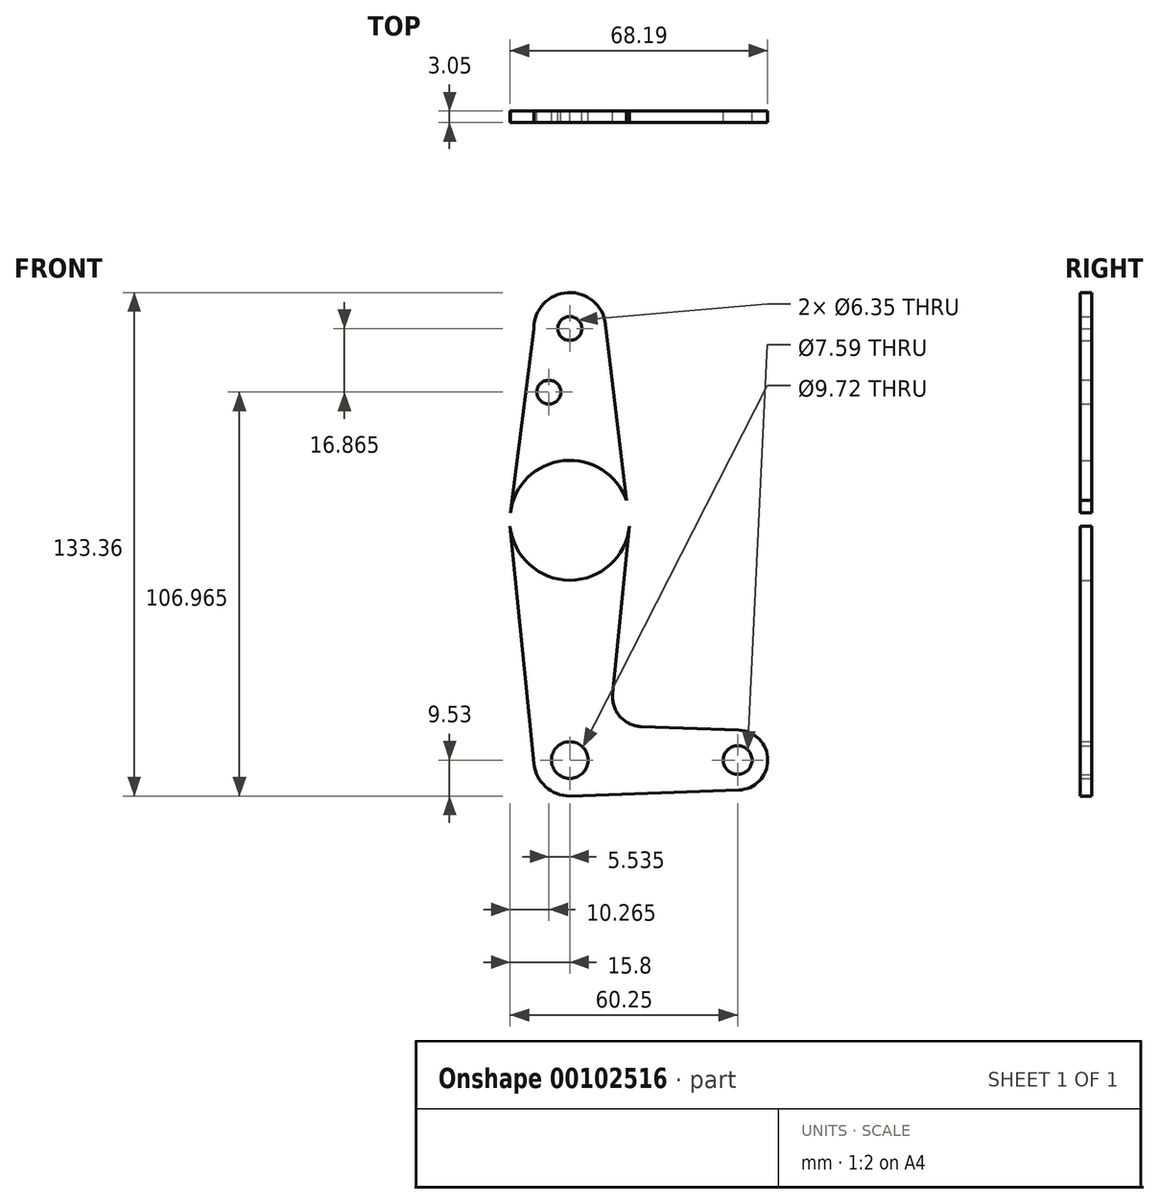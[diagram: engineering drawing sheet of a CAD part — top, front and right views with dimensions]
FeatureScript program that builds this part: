
annotation { "Feature Type Name" : "Feature", "Feature Type Description" : "" }
export const myFeature = defineFeature(function(context is Context, id is Id, definition is map)
    precondition{}
    {
        {
            var Q0;
            Q0=qCreatedBy(makeId("Front.planeOp"),FACE);
            var sketch = newSketch(context, id + "F0", { "sketchPlane" : qUnion([Q0])});
            skLineSegment(sketch, "E0", {"start": v(0, 114.3) * mm, "end": v(0, 0) * mm});
            skLineSegment(sketch, "E1", {"start": v(0, 0) * mm, "end": v(83.2, 0) * mm});
            skCircle(sketch, "E2", {"center": v(0, 114.3) * mm, "radius": 9.53 * mm});
            skCircle(sketch, "E3", {"center": v(0, 63.5) * mm, "radius": 15.88 * mm});
            skCircle(sketch, "E4", {"center": v(44.45, 0) * mm, "radius": 7.94 * mm});
            skCircle(sketch, "E5", {"center": v(0, 0) * mm, "radius": 9.53 * mm});
            skLineSegment(sketch, "E6", {"start": v(15.8, 61.91) * mm, "end": v(11.34, 17.59) * mm});
            skLineSegment(sketch, "E7", {"start": v(15.8, 61.91) * mm, "end": v(9.46, 115.42) * mm});
            skLineSegment(sketch, "E8", {"start": v(-9.53, 114.3) * mm, "end": v(-15.75, 65.5) * mm});
            skLineSegment(sketch, "E9", {"start": v(-15.8, 61.91) * mm, "end": v(-9.48, -0.95) * mm});
            skLineSegment(sketch, "E10", {"start": v(18.97, 8.85) * mm, "end": v(44.73, 7.93) * mm});
            skLineSegment(sketch, "E11", {"start": v(0, -9.53) * mm, "end": v(44.73, -7.93) * mm});
            skCircle(sketch, "E12", {"center": v(-5.53, 97.43) * mm, "radius": 3.18 * mm});
            skCircle(sketch, "E13", {"center": v(0, 114.3) * mm, "radius": 3.18 * mm});
            skCircle(sketch, "E14", {"center": v(0, 63.5) * mm, "radius": 1.59 * mm});
            skCircle(sketch, "E15", {"center": v(0, 0) * mm, "radius": 4.86 * mm});
            skCircle(sketch, "E16", {"center": v(44.45, 0) * mm, "radius": 3.8 * mm});
            skArc(sketch, "E17.filletArc", {"start": v(11.34, 17.59) * mm, "mid": v(13.26, 11.57) * mm, "end": v(18.97, 8.85) * mm});
            skSolve(sketch);
        }
        {
            var Q0;
            {var subQ0=sQuery(id+"F0.wireOp",EDGE,"E2");var subQ1=sQuery(id+"F0.wireOp",EDGE,"E0");var subQ2=makeQuery(id+"F0.imprint","INTERSECT",VERTEX,{"derivedFrom":[subQ1,subQ0]});Q0=makeQuery(id+"F0.imprint","IMPRINT",FACE,{"disambiguationData":[TD([[makeQuery(id+"F0.imprint","IMPRINT",EDGE,{"disambiguationData":[TD([[subQ2,-1.0]])],"derivedFrom":subQ1}),1.0]])]});}
            var Q1;
            Q1=makeQuery(id+"F0.imprint","IMPRINT",FACE,{"disambiguationData":[TD([[makeQuery(id+"F0.imprint","IMPRINT",EDGE,{"derivedFrom":sQuery(id+"F0.wireOp",EDGE,"E13")}),-1.0]])]});
            var Q2;
            {var subQ1=sQuery(id+"F0.wireOp",EDGE,"E3");var subQ3=sQuery(id+"F0.wireOp",EDGE,"E0");var subQ6=makeQuery(id+"F0.imprint","INTERSECT",VERTEX,{"disambiguationData":[OD(0.0)],"derivedFrom":[subQ3,subQ1]});Q2=makeQuery(id+"F0.imprint","IMPRINT",FACE,{"disambiguationData":[TD([[makeQuery(id+"F0.imprint","IMPRINT",EDGE,{"disambiguationData":[TD([[subQ6,-1.0]])],"derivedFrom":subQ3}),1.0]])]});}
            var Q3;
            {var subQ0=sQuery(id+"F0.wireOp",EDGE,"E3");var subQ4=sQuery(id+"F0.wireOp",EDGE,"E0");var subQ7=makeQuery(id+"F0.imprint","INTERSECT",VERTEX,{"disambiguationData":[OD(0.0)],"derivedFrom":[subQ4,subQ0]});Q3=makeQuery(id+"F0.imprint","IMPRINT",FACE,{"disambiguationData":[TD([[makeQuery(id+"F0.imprint","IMPRINT",EDGE,{"disambiguationData":[TD([[subQ7,-1.0]])],"derivedFrom":subQ4}),-1.0]])]});}
            var Q4;
            {var subQ5=sQuery(id+"F0.wireOp",EDGE,"E9");Q4=makeQuery(id+"F0.imprint","IMPRINT",FACE,{"disambiguationData":[TD([[makeQuery(id+"F0.imprint","IMPRINT",EDGE,{"derivedFrom":subQ5}),1.0]])]});}
            var Q5;
            {var subQ4=sQuery(id+"F0.wireOp",EDGE,"E6");Q5=makeQuery(id+"F0.imprint","IMPRINT",FACE,{"disambiguationData":[TD([[makeQuery(id+"F0.imprint","IMPRINT",EDGE,{"derivedFrom":subQ4}),-1.0]])]});}
            var Q6;
            {var subQ0=sQuery(id+"F0.wireOp",EDGE,"E5");var subQ1=sQuery(id+"F0.wireOp",EDGE,"E0");var subQ2=makeQuery(id+"F0.imprint","INTERSECT",VERTEX,{"derivedFrom":[subQ1,subQ0]});Q6=makeQuery(id+"F0.imprint","IMPRINT",FACE,{"disambiguationData":[TD([[makeQuery(id+"F0.imprint","IMPRINT",EDGE,{"disambiguationData":[TD([[subQ2,-1.0]])],"derivedFrom":subQ1}),1.0]])]});}
            var Q7;
            {var subQ0=sQuery(id+"F0.wireOp",EDGE,"E5");var subQ4=sQuery(id+"F0.wireOp",EDGE,"E0");var subQ5=makeQuery(id+"F0.imprint","INTERSECT",VERTEX,{"derivedFrom":[subQ4,subQ0]});Q7=makeQuery(id+"F0.imprint","IMPRINT",FACE,{"disambiguationData":[TD([[makeQuery(id+"F0.imprint","IMPRINT",EDGE,{"disambiguationData":[TD([[subQ5,-1.0]])],"derivedFrom":subQ4}),-1.0]])]});}
            var Q8;
            {var subQ0=sQuery(id+"F0.wireOp",EDGE,"E5");var subQ1=sQuery(id+"F0.wireOp",EDGE,"E1");var subQ2=makeQuery(id+"F0.imprint","INTERSECT",VERTEX,{"derivedFrom":[subQ1,subQ0]});Q8=makeQuery(id+"F0.imprint","IMPRINT",FACE,{"disambiguationData":[TD([[makeQuery(id+"F0.imprint","IMPRINT",EDGE,{"disambiguationData":[TD([[subQ2,-1.0]])],"derivedFrom":subQ1}),-1.0]])]});}
            var Q9;
            {var subQ0=sQuery(id+"F0.wireOp",EDGE,"E4");var subQ2=sQuery(id+"F0.wireOp",EDGE,"E1");var subQ6=makeQuery(id+"F0.imprint","INTERSECT",VERTEX,{"disambiguationData":[OD(1.0)],"derivedFrom":[subQ2,subQ0]});Q9=makeQuery(id+"F0.imprint","IMPRINT",FACE,{"disambiguationData":[TD([[makeQuery(id+"F0.imprint","IMPRINT",EDGE,{"disambiguationData":[TD([[subQ6,-1.0]])],"derivedFrom":subQ2}),-1.0]])]});}
            var Q10;
            {var subQ0=sQuery(id+"F0.wireOp",EDGE,"E4");var subQ2=sQuery(id+"F0.wireOp",EDGE,"E1");var subQ4=makeQuery(id+"F0.imprint","INTERSECT",VERTEX,{"disambiguationData":[OD(1.0)],"derivedFrom":[subQ2,subQ0]});Q10=makeQuery(id+"F0.imprint","IMPRINT",FACE,{"disambiguationData":[TD([[makeQuery(id+"F0.imprint","IMPRINT",EDGE,{"disambiguationData":[TD([[subQ4,-1.0]])],"derivedFrom":subQ2}),1.0]])]});}
            var Q11;
            {var subQ0=sQuery(id+"F0.wireOp",EDGE,"E8");Q11=makeQuery(id+"F0.imprint","IMPRINT",FACE,{"disambiguationData":[TD([[makeQuery(id+"F0.imprint","IMPRINT",EDGE,{"derivedFrom":subQ0}),1.0]])]});}
            extrude(context, id + "F1", {"entities" : qUnion([Q0, Q1, Q2, Q3, Q4, Q5, Q6, Q7, Q8, Q9, Q10, Q11]), "depth" : 3.05 * mm});
        }
    });
